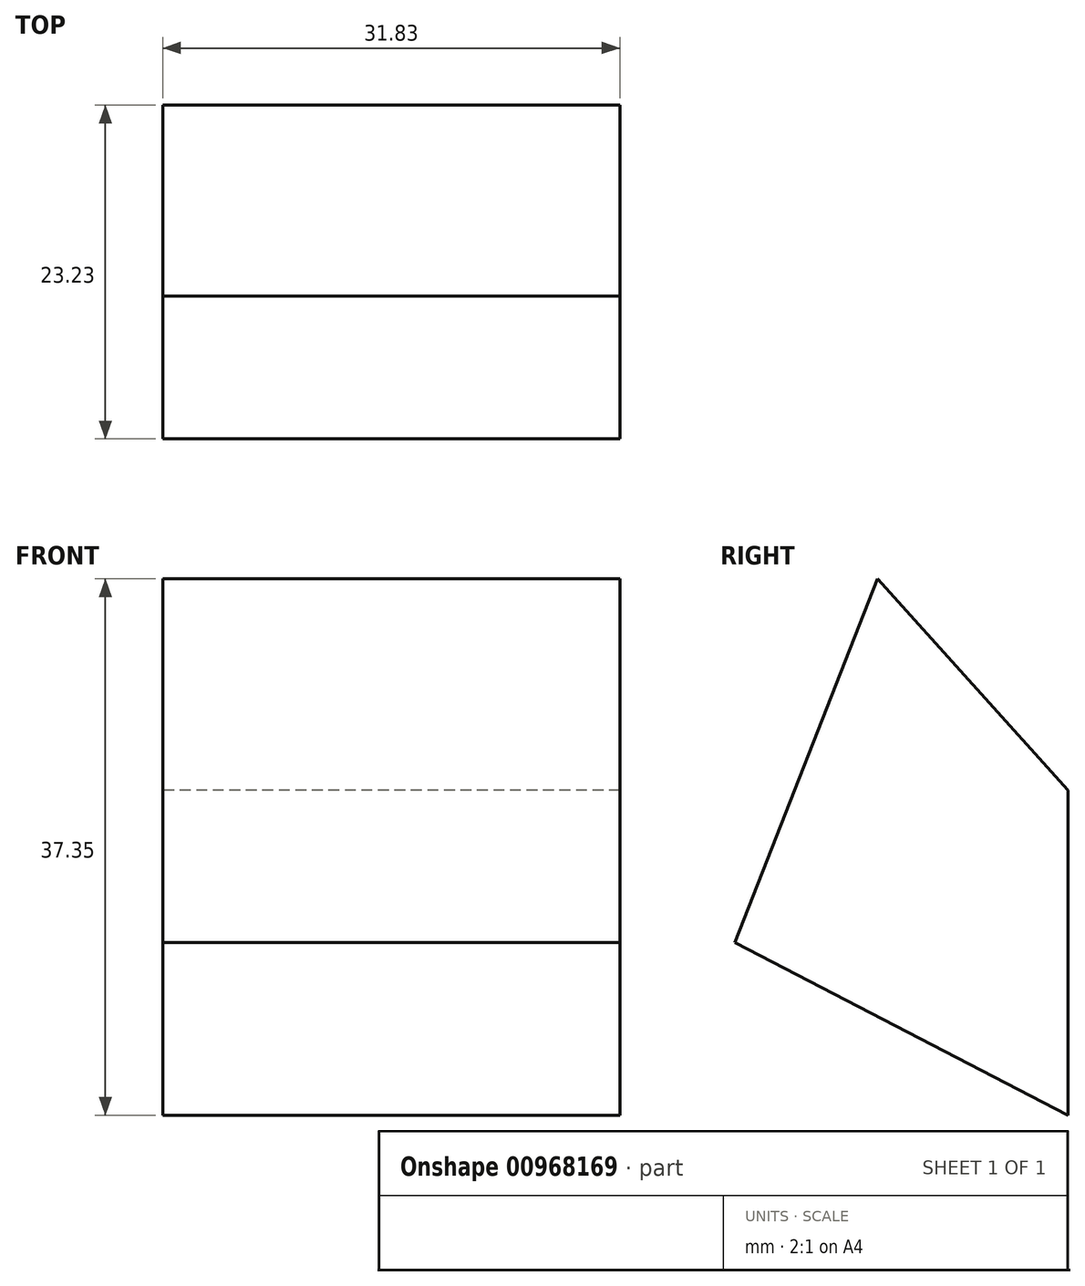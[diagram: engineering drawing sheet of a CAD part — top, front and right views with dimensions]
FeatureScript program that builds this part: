
annotation { "Feature Type Name" : "Feature", "Feature Type Description" : "" }
export const myFeature = defineFeature(function(context is Context, id is Id, definition is map)
    precondition{}
    {
        {
            var Q0;
            Q0=qCreatedBy(makeId("Right.planeOp"),FACE);
            var sketch = newSketch(context, id + "F0", { "sketchPlane" : qUnion([Q0])});
            skLineSegment(sketch, "E0", {"start": v(36.3, 20.95) * mm, "end": v(36.3, 43.57) * mm});
            skLineSegment(sketch, "E1", {"start": v(36.3, 43.57) * mm, "end": v(23.03, 58.3) * mm});
            skLineSegment(sketch, "E2", {"start": v(23.03, 58.3) * mm, "end": v(13.07, 32.99) * mm});
            skLineSegment(sketch, "E3", {"start": v(13.07, 32.99) * mm, "end": v(36.3, 20.95) * mm});
            skSolve(sketch);
        }
        {
            var Q0;
            Q0 = qSketchRegion(id + "F0", true);
            extrude(context, id + "F1", {"entities" : qUnion([Q0]), "depth" : 31.83 * mm, "offsetDistance" : 25.4 * mm});
        }
    });
